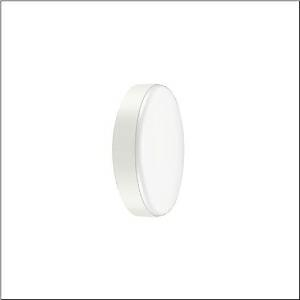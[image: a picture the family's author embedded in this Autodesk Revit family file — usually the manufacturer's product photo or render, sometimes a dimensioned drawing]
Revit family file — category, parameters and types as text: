
# Revit family: round_31_51wc10ma32as
name_source: partatom
category: Lighting Fixtures
units: mm (PartAtom-declared; Revit-internal decimal feet)

## family parameters
Cut with Voids When Loaded = No
Host = Face
Light Source = No
Part Type = Normal
Room Calculation Point = No
Round Connector Dimension = Use Diameter
Shared = No

## types (1)
- --- (1 x LED, 2450 lm, 20.4 W, 3000K)
    Apparent Load = 20 VA
    CIE Flux Codes = 44 75 94 94 100
    Color Rendering = 80
    Color Temperature = 3000K
    Default Elevation = 1800 mm
    Description = Round 31, wall and ceiling luminaire, primary optical cover: cover, of PC, opal, light emission: direct distribution, primary light characteristic: symmetric, installation type: surface-mounted, LED, rated luminous flux: 2.450lm, luminous efficacy: 120lm/W, light colour: 830, colour temperature: 3000K, control gear: ON/OFF Multilumen, with terminal, 3-pole, max. 2.5mm², mains connection: 220..240V, AC, 50/60Hz, rated input power: 20.5W, luminaire housing, of PC, traffic white (RAL 9016), diameter: 350mm, brightness and presence sensor, HF sensor, protection rating (complete): IP65, insulation class (complete): insulation class II (safety insulation), certification: CE, impact resistance: IK10, permissible operating ambient temperature: -20..+40°C, permissible storage temperature: -20..+60°C, packaging unit: 1 piece
    Height = 97 mm
    Lamp = 1 x LED
    Lamp Light Flux = 2450 lm
    Lamp Power = 20.4 W
    Lamp count = 1
    Length = 350 mm
    Luminous efficacy = 120 lm/W
    Manufacturer = Siteco
    ModVariant = No
    Model = 51WC10MA32AS
    Mounting Place = Wall
    Mounting Type = Surface mounted
    Number of Poles = 1
    OnlyDefault = Yes
    Power Factor = 1
    Product Name = Round 31
    Product group = wall and ceiling luminaire | wall mounted
    ProductGroupID = 2001
    Protection Class = Protection class II
    Protection Degree = IP 65
    RLX_Detail_Level = 1
    RLX_Emergency_Light_Flux = 0 lm
    RLX_Emergency_Type = 0
    RLX_Emergency_Type_DB = No
    RlxData = <blob elided: 30421 chars, md5=2b704b88>
    Socket = socket
    Standby Power = 0 W
    System Light Flux = 2450 lm
    System Power = 20 W
    Type Comments = factory setting: luminous flux: 100 % | (ON | ON)
    Type Image = l_1007027.jpg
    URL = http://relux.com
    VarID = @adj_111805
    Voltage = 0 V
    Weight = 0.00 kg
    Width = 0 mm  [stored 0 ft]

note: [stored X ft] marks values corroborated as IEEE doubles in the binary element streams (Revit-internal decimal feet)

## geometry (parser evidence)
native form markers: Blend x4, Sweep x13
no freeform markers — native parametric forms only
